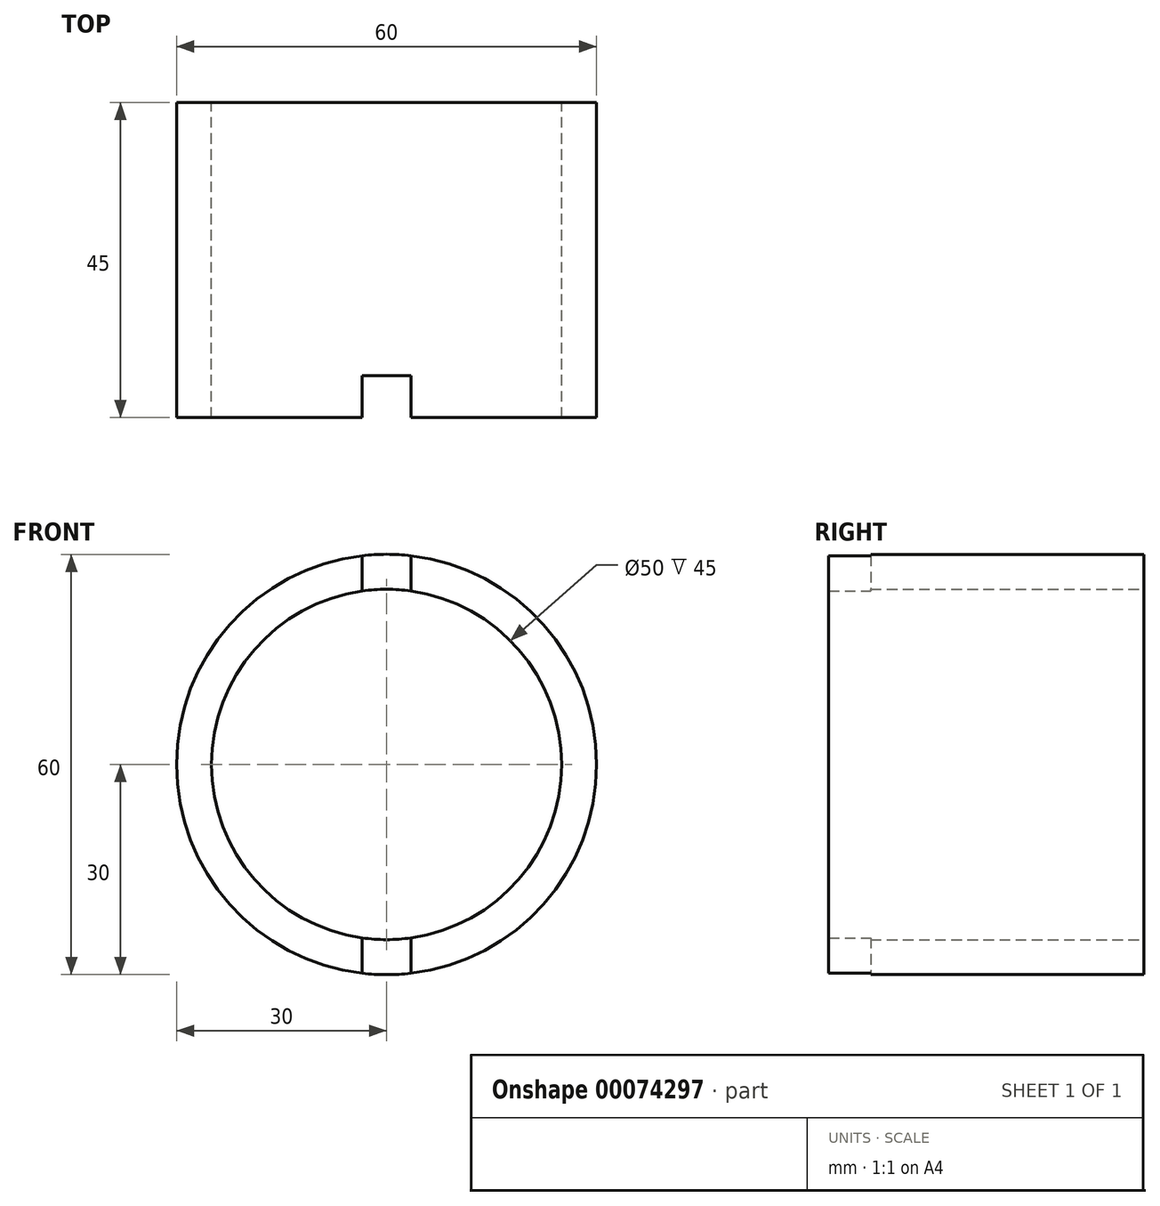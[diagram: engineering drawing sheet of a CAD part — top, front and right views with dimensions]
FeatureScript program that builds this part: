
annotation { "Feature Type Name" : "Feature", "Feature Type Description" : "" }
export const myFeature = defineFeature(function(context is Context, id is Id, definition is map)
    precondition{}
    {
        {
            var Q0;
            Q0=qCreatedBy(makeId("Front.planeOp"),FACE);
            var sketch = newSketch(context, id + "F0", { "sketchPlane" : qUnion([Q0])});
            skCircle(sketch, "E0", {"center": v(0, 0) * mm, "radius": 30 * mm});
            skCircle(sketch, "E1", {"center": v(0, 0) * mm, "radius": 25 * mm});
            skSolve(sketch);
        }
        {
            var Q0;
            Q0 = qSketchRegion(id + "F0", true);
            extrude(context, id + "F1", {"entities" : qUnion([Q0]), "depth" : 45 * mm});
        }
        {
            var Q0;
            Q0=makeQuery(id+"F1.opExtrude","CAP_FACE",FACE,{"disambiguationData":[OSD([sQuery(id+"F0.wireOp",EDGE,"E0"),sQuery(id+"F0.wireOp",EDGE,"E1")])],"isStart":false});
            var sketch = newSketch(context, id + "F2", { "sketchPlane" : qUnion([Q0])});
            skLineSegment(sketch, "E2", {"start": v(0, -34.77) * mm, "end": v(0, 36.07) * mm, "construction": true});
            skLineSegment(sketch, "E3", {"start": v(-3.5, 39.67) * mm, "end": v(-3.5, -34.77) * mm});
            skLineSegment(sketch, "E4", {"start": v(-3.5, 39.67) * mm, "end": v(3.5, 39.67) * mm});
            skLineSegment(sketch, "E5", {"start": v(3.5, 39.67) * mm, "end": v(3.5, -34.77) * mm});
            skLineSegment(sketch, "E6", {"start": v(3.5, -34.77) * mm, "end": v(-3.5, -34.77) * mm});
            skSolve(sketch);
        }
        {
            var Q0;
            Q0 = qSketchRegion(id + "F2", true);
            extrude(context, id + "F3", {"entities" : qUnion([Q0]), "operationType" : NewBodyOperationType.REMOVE, "oppositeDirection" : true, "depth" : 6 * mm});
        }
    });
